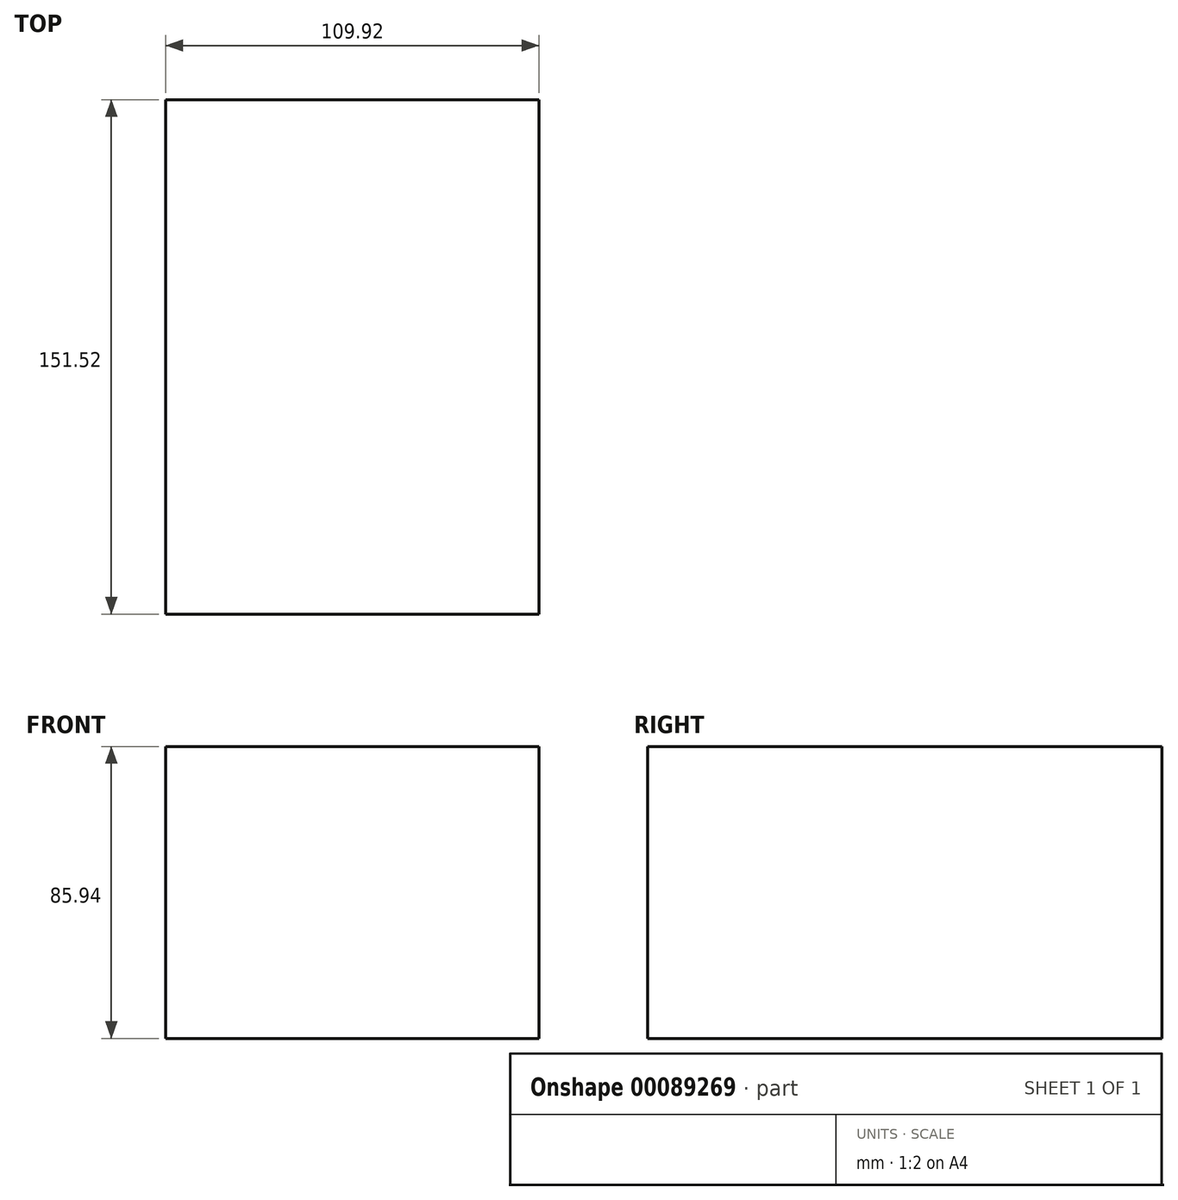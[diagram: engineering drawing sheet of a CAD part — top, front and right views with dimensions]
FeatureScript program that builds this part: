
annotation { "Feature Type Name" : "Feature", "Feature Type Description" : "" }
export const myFeature = defineFeature(function(context is Context, id is Id, definition is map)
    precondition{}
    {
        {
            var Q0;
            Q0=qCreatedBy(makeId("Front.planeOp"),FACE);
            var sketch = newSketch(context, id + "F0", { "sketchPlane" : qUnion([Q0])});
            skLineSegment(sketch, "E0", {"start": v(-109.92, 0) * mm, "end": v(0, 0) * mm});
            skLineSegment(sketch, "E1", {"start": v(0, 0) * mm, "end": v(0, -85.94) * mm});
            skLineSegment(sketch, "E2", {"start": v(0, -85.94) * mm, "end": v(-109.92, -85.94) * mm});
            skLineSegment(sketch, "E3", {"start": v(-109.92, -85.94) * mm, "end": v(-109.92, 0) * mm});
            skSolve(sketch);
        }
        {
            var Q0;
            Q0=makeQuery(id+"F0.imprint","IMPRINT",FACE,{"disambiguationData":[TD([[makeQuery(id+"F0.imprint","IMPRINT",EDGE,{"derivedFrom":sQuery(id+"F0.wireOp",EDGE,"E0")}),-1.0]])]});
            extrude(context, id + "F1", {"entities" : qUnion([Q0]), "depth" : 151.52 * mm});
        }
    });
